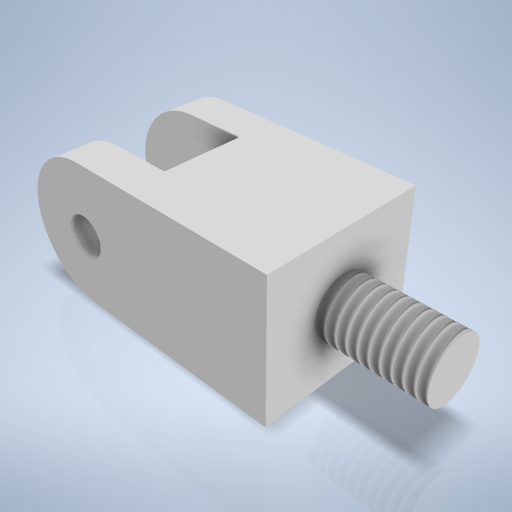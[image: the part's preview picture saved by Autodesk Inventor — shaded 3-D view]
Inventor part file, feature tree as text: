
AUTODESK INVENTOR PART (.ipt)
format: ipt  version: 2024.2 (Build 282272000, 272)  size: 281,088 bytes
history: native  units: mm
features: sketch x4, extrude x3, fillet x1, hole x1, thread x1
ambient origin geometry x8: Origin, YZ Plane, XZ Plane, XY Plane, X Axis, Y Axis, Z Axis, Center Point
bodies: Volumenkörper1 (feature_tree)
feature tree (10):
  extrude  "Extrusion1"  Depth=8.0mm
  fillet  "Rundung1"  Radius=8.0mm
  hole  "Bohrung1"  [1 undecoded]
  extrude  "Extrusion2"  Depth=2.0mm
  extrude  "Extrusion3"  Depth=8.0mm TaperAngle=0.0deg
  thread  "Gewinde1"  [1 undecoded]
  sketch  "Skizze1"  dims[d0=7.0mm d1=14.0mm d2=8.0mm d3=0.0mm]
  sketch  "Skizze2"  dims[d4=3.5mm]
  sketch  "Skizze3"  dims[d5=2.0mm d6=1.5mm d7=4.0mm d8=2.0mm d9=90.0deg d10=1.5mm d11=0.0mm d12=6.5mm]
  sketch  "Skizze4"  dims[d13=4.0mm d14=2.0mm d15=8.0mm d16=0.0mm d17=3.0mm d18=5.0mm d19=0.0mm d20=18.0mm d21=0.0mm]
note: 2 required parameter values undecoded (feature->parameter linkage not recoverable at this tier; creation-order binding heuristic only, values carry confidence <= 0.55)
